# Revit family: HD127-2016.10.03-BT-SS-Woodbrise66
name_source: partatom
category: Modelos genéricos
revit_build: Autodesk Revit 2017 (Build: 20160225_1515(x64)
units: mm (PartAtom-declared; Revit-internal decimal feet)

## family parameters
Compartido = No
Corte con vacíos al cargar = No
Cota de conector redondo = Diámetro de uso
Puede alojar armadura = No
Punto de cálculo de habitación = No
Se basa en plano de trabajo = No
Siempre vertical = Sí
Tipo de pieza = Normal

## types (1)
- Productos HD
    BT_Alto = 25 mm
    BT_Ancho = 66 mm
    BT_Codigo_Origen = HD127
    BT_Color = Para uso interior: sellante y laca con teñidos: miel, california-oak y café moro
    BT_Código_Línea = De Linea
    BT_Descripcion = Quiebravista Woodbrise 66
    BT_EETT = Las tapas de aluminio, resistentes al impacto e intemperie, llevan un ala integrada que
se une a la barra de accionamiento (opción móvil), que permite el movimiento giratorio
manual o por medio de un motor eléctrico. La opción fija permite predeterminar el ángulo
de inclinación de las paletas. Éstas quedan fijas en el ángulo deseado. La sustentación del
quiebravista Woodbrise se efectúa mediante perfiles de aluminio extruído,donde descansan las paletas. Estos perfiles de aluminio se fijan a la
estructura mediante soportes, escuadras u otros elementos diseñados especialmente para
cada caso o necesidad.
    BT_Elemento = Celosías y Quiebravistas
    BT_Especialidad = Arquitectura
    BT_Fabricante = Hunter Douglas
    BT_Itemizado_Estandar_CDT = D 01 08 80
    BT_Marca = Hunter Douglas
    BT_MasterFormat® = 08 91 19
    BT_Material = Aluminio prepintado
    BT_Nombre_Corto = Quiebravista Woodbrise 66
    BT_Nombre_Tecnico = Quiebravista Woodbrise 66
    BT_Peso = Mañío: 6,6 Kg/m2, Cedro: 4.8 Kg/m2
    BT_Profundidad = Largo Máximo según proyecto
    BT_SKU = 00 20 58
    BT_Uso = Interior y Exterior
    BT_Web_del_Producto = http://www.hunterdouglas.cl
    ID_Objeto = BT_F_F_749
    ID_Source = BIMTOOL
    Material = Metal

## geometry (parser evidence)
native form markers: Sweep x114
no freeform markers — native parametric forms only
